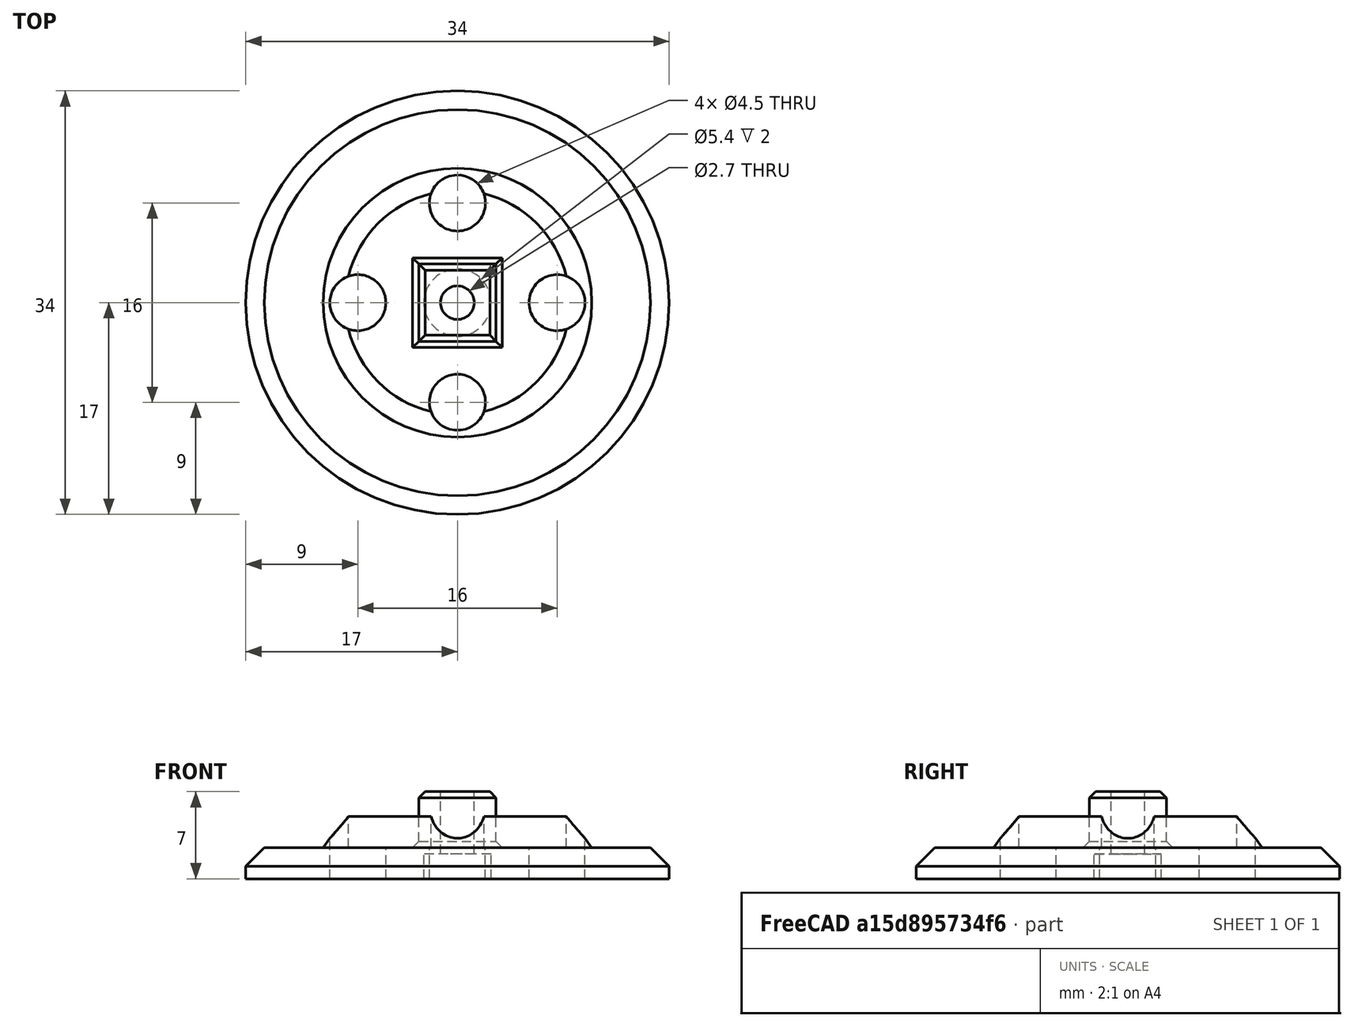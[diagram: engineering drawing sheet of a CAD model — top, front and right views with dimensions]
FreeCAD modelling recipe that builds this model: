
FCSTD DOCUMENT  (FreeCAD 0.16R6705 (Git))
Label: tendon_wheel_ax_9_17_mm_top
License: CC-BY 3.0
LicenseURL: http://creativecommons.org/licenses/by/3.0/
objects: Part::Cylinder×8, Part::MultiFuse×4, Part::Cut×3, Part::Chamfer×3, Part::Cone×1, Part::Box×1
note: 20 computed .brp shape members not serialized (recipe doc carries the construction recipe); baked Part::Feature solids carry a one-line shape summary decoded from their .brp

FEATURE [Part::Cylinder] Cylinder
  Angle = 360
  Height = 6
  Placement = pos=(0,0,2) rot=(0,0,1;0rad)
  Radius = 9
FEATURE [Part::Cylinder] Cylinder001
  Angle = 360
  Height = 2.5
  Placement = pos=(0,0,-0.5) rot=(0,0,1;0rad)
  Radius = 17
FEATURE [Part::Cone] Cone
  Angle = 360
  Height = 3.5
  Placement = pos=(0,0,1) rot=(0,0,1;0rad)
  Radius1 = 11.5
  Radius2 = 9
FEATURE [Part::Box] Box  label="Cube"
  Height = 4.5
  Length = 6.2
  Placement = pos=(-3.1,-3.1,2) rot=(0,0,1;0rad)
  Width = 6.2
FEATURE [Part::MultiFuse] Fusion
  Shapes = -> [Cone,Cylinder001]
FEATURE [Part::Cylinder] Cylinder002  label="Cylinder004"
  Angle = 360
  Height = 20
  Placement = pos=(0,0,-5) rot=(0,0,1;0rad)
  Radius = 1.35
FEATURE [Part::Cut] Cut
  Base = -> Fusion
  Tool = -> Cylinder
FEATURE [Part::MultiFuse] Fusion001
  Shapes = -> [Cut,Box]
FEATURE [Part::Cylinder] Cylinder003  label="Cylinder012"
  Angle = 360
  Height = 2
  Placement = pos=(0,0,-0.5) rot=(0,0,1;0rad)
  Radius = 2.7
FEATURE [Part::MultiFuse] Fusion002
  Shapes = -> [Cylinder003,Cylinder002]
FEATURE [Part::Cut] Cut001
  Base = -> Fusion001
  Tool = -> Fusion002
FEATURE [Part::Chamfer] Chamfer
  Base = -> Cut001
  Edges = 4 edges r=0.5: [Edge1,Edge2,Edge3,Edge4]
FEATURE [Part::Cylinder] Cylinder005  label="TopHole005"
  Angle = 360
  Height = 20
  Placement = pos=(8,0,-4) rot=(0,0,1;0rad)
  Radius = 2.25
FEATURE [Part::Cylinder] Cylinder008  label="TopHole006"
  Angle = 360
  Height = 20
  Placement = pos=(0,8,-4) rot=(0,0,1;0rad)
  Radius = 2.25
FEATURE [Part::Cylinder] Cylinder009  label="TopHole004"
  Angle = 360
  Height = 20
  Placement = pos=(-8,0,-4) rot=(0,0,1;0rad)
  Radius = 2.25
FEATURE [Part::Cylinder] Cylinder011  label="TopHole007"
  Angle = 360
  Height = 20
  Placement = pos=(0,-8,-4) rot=(0,0,1;0rad)
  Radius = 2.25
FEATURE [Part::MultiFuse] Fusion003
  Shapes = -> [Cylinder011,Cylinder008,Cylinder009,Cylinder005]
FEATURE [Part::Cut] Cut002
  Base = -> Chamfer
  Tool = -> Fusion003
FEATURE [Part::Chamfer] Chamfer001
  Base = -> Cut002
  Edges = 4 edges r=0.5: [Edge17,Edge20,Edge22,Edge23]
FEATURE [Part::Chamfer] Chamfer002
  Base = -> Chamfer001
  Edges = 1 edges r=1.5: [Edge73]
